# Revit family: replaced_Water_Cooler-Bottle_Filler-Wall_Mounted-Acorn-Murdock-AL81408S
name_source: partatom
category: Plumbing Fixtures
revit_build: Autodesk Revit MEP 2016 (Build: 20150220_1215(x64)
units: mm (PartAtom-declared; Revit-internal decimal feet)

## family parameters
Cut with Voids When Loaded = No
Host = Face
OmniClass Number = 23.65.70.14.11
OmniClass Title = Drinking Fountains/Coolers
Part Type = Normal
Room Calculation Point = No
Round Connector Dimension = Use Diameter
Shared = Yes

## types (1)
- AL81408S
    220V 220 Volt/50 Hz or 60 Hz Compressor = No
    Assembly Code = D2010810
    BF Ligature Resistant Bottle/Cup Filler = No
    CW Connection = Yes
    CWFU = 1.5
    Connection Size = 1 1/4"
    Default Elevation = 51 3/4"
    Description = This 16-gauge stainless steel recessed fountain is designed with ligature-resistant features including bubbler, drain, and bottle filler spout. Water is chilled with an in-wall chiller rated at 8 GPH.
    Finish = Metal-Murdock-Stainless Steel-Type 304-Satin
    GPH = 8.0 GPH
    HW Connection = No
    HWFU = 0
    Height = 56 3/4"
    Inlet Diameter Connection = 3/8"
    Installation Type = FULLY RECESSED, WALL MOUNTED
    LBPH Less Bubbler & Less Bubbler Pushbutton Actuator = No
    Length = 12"
    Load Rating = 4.6 Full Load Amps
    Manufacturer = Murdock
    Material = Metal-Murdock-Stainless Steel-Type 304-Satin
    Model = AL81408S
    Product Documentation Link = https://www.murdockmfg.com
    Product Page URL = https://www.murdockmfg.com
    Specification = Model AL81408S is a self-contained, Ligature Resistant, fully recessed pressure electric Drinking Fountain that shall deliver a minimum of 8.0 GPH (30.3 LPH) of water at 50°F (10°C) cooled from 80°F (26.7°C) inlet water and 90°F (32.2°C) ambient. Unit shall be activated by a brass, chrome plated front Pushbutton using less then 5 pounds of force. Bubbler shall be Stainless Steel, Ligature Resistant and operate on a water pressure range of 20-105 PSIG. Cabinet Panels shall be constructed from 304 Stainless Steel and the Bowl shall have an integral Ligature Resistant Drain. Cooling system shall use R-134a refrigerant and be capillary tube regulated. An adjustable Thermostat with an off position shall regulate the Refrigeration System. Unit shall be listed by Underwriters Laboratories for both the US and Canada and is compliant to the Air Conditioning and Refrigeration Institute Standard 1010. Unit is certified to ANSI A117.1, Public Law 111-380 (NO-LEAD), CHSC 116875 and NSF/ANSI 61, Section 9. Unit shall Still deliver ambient water temperature to the Bubbler in the absence of electrical
power as long as there is a pressurized water supply.
    Tempered Water Connection = No
    URL = http://www.murdockmfg.com
    Vent Connection = No
    WF1 1500-Gallon Capacity, NSF 42+53, = No
    WF3 3000-Gallon Capacity, NSF 42+53, 1-Micron Lead Reduction Filter = No
    WFU = 2
    Warranty Documentation Link = https://www.murdockmfg.com
    Waste Connection = Yes
    Watts = 390 W
    Weight Lbs = 110 lbs.
    Width = 19"

## geometry (parser evidence)
native form markers: Sweep x2
no freeform markers — native parametric forms only
